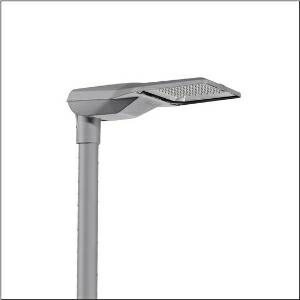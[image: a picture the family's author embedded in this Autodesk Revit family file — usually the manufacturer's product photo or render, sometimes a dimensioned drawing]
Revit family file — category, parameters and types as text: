
# Revit family: streetlight_sl_21_iq_midi___st1_0a_5xe3d21g08nb_5ac0
name_source: partatom
category: Lighting Fixtures
units: mm (PartAtom-declared; Revit-internal decimal feet)

## family parameters
Cut with Voids When Loaded = No
Host = Face
Light Source = No
Part Type = Normal
Room Calculation Point = No
Round Connector Dimension = Use Diameter
Shared = No

## types (1)
- --- (1 x LED, 19210 lm, 155.5 W, 2200K)
    Apparent Load = 155 VA
    CIE Flux Codes = 40 73 97 100 100
    Color Rendering = 70
    Color Temperature = 2200K
    Default Elevation = 1800 mm
    Description = Streetlight SL 21 iQ midi, mast luminaire, primary light control with lens, of PMMA, primary optical cover: cover, of toughened safety glass, transparent, light distribution: ST1.0a, light emission: direct distribution, primary light characteristic: asymmetric, installation type: post-top, side-entry, LED, High Power LED, rated luminous flux: 19.210lm, luminous efficacy: 124lm/W, light colour: 722, colour temperature: 2200K, control gear: iQ Street-Remote, control: Street-Remote, Auto-Match, Temp-Guard, Lumen-Switch, Night-Set, Smart-Wire, Light-Fading, Desk-Remote (wireless, voltage-free reading and setting of iQ features in the workshop via application-optimized NFC function/RFID function), optimised constant luminous flux control (CLO 2.0), pre-setting: linear dimming characteristic, mains connection: 230..240V, AC, 50/60Hz, start of lifetime: 156W, end of service life: 162W, reduction: 69W, luminaire housing, of diecast aluminium, powder-coated, Siteco® metallic grey (DB 702S), corrosivity category C5 mid according to DIN EN ISO 12944, please order mast flange separately, inclination adjustable: 0°, 5°, 10°, 15°, sealing non-destructively replaceable, multi-level sealing system, length: 644mm, width: 335mm, height: 110mm, mast flange for spigot size: 42mm (side-entry): 5XC10008XM4, 60/48mm (side-entry/post-top): 5XC10108XM2, 76/60mm (side-entry/post-top): 5XC10108XM1, mounting height: 4..8m, protection rating (complete): IP66, insulation class (complete): insulation class II (safety insulation), certification: CE, ENEC, ENEC+, VDE, impact resistance: IK10, permissible operating ambient temperature for outdoor applications: -40..+50°C, standard-compliant lighting for roads and squares, packaging unit: 1 piece

Light Distribution: ST1.0a
    Height = 111 mm
    Lamp = 1 x LED
    Lamp Light Flux = 19210 lm
    Lamp Power = 155.5 W
    Lamp count = 1
    Length = 644 mm
    Luminous efficacy = 124 lm/W
    Manufacturer = Siteco
    ModVariant = No
    Model = 5XE3D21G08NB
    Number of Poles = 1
    OnlyDefault = Yes
    Power Factor = 1
    Product Name = Streetlight SL 21 iQ midi | ST1.0a
    Product group = mast luminaire | pylon top
    ProductGroupID = 6100
    Protection Class = Protection class II
    Protection Degree = IP 66
    RLX_Detail_Level = 1
    RLX_Emergency_Light_Flux = 0 lm
    RLX_Emergency_Type = 0
    RLX_Emergency_Type_DB = No
    RlxData = <blob elided: 27217 chars, md5=bcafa890>
    Socket = socket
    Standby Power = 0 W
    System Light Flux = 19210 lm
    System Power = 155 W
    Type Comments = factory setting: luminous flux: 100 % | dim-lin: 254 | 823 mA
    Type Image = l_1004298.jpg
    URL = http://relux.com
    VarID = @adj_192395
    Voltage = 0 V
    Weight = 0.00 kg
    Width = 336 mm

## geometry (parser evidence)
native form markers: Blend x4, Sweep x10
no freeform markers — native parametric forms only
